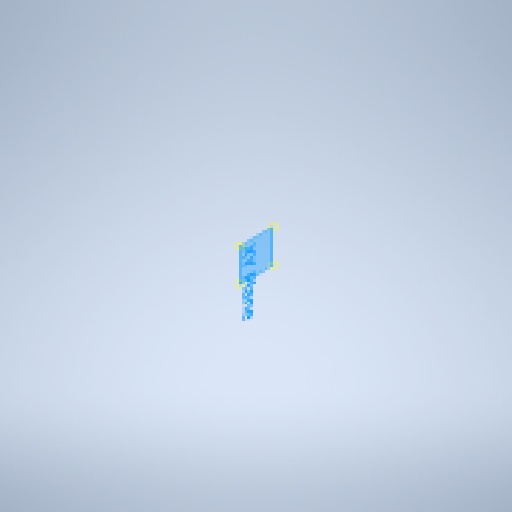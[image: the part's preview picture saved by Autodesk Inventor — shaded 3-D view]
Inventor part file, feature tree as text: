
AUTODESK INVENTOR PART (.ipt)
format: ipt  version: 2023 (Build 270158000, 158)  size: 151,040 bytes
history: native  units: mm
features: other x3, extrude x2, sketch x2, plane x1, chamfer x1, reference x1
ambient origin geometry x8: Origin, YZ Plane, XZ Plane, XY Plane, X Axis, Y Axis, Z Axis, Center Point
bodies: Solid1 (feature_tree)
feature tree (10):
  plane  "Work Plane1"
  extrude  "Extrusion1"  Depth=24.6mm
  extrude  "Extrusion2"  Depth=2.4mm TaperAngle=30.0deg
  chamfer  "Chamfer1"  [1 undecoded]
  sketch  "Sketch1"  dims[d0=24.6mm d1=0.0mm d2=5.9mm]
  reference  "Reference1"
  sketch  "Sketch2"  dims[d3=2.4mm d4=0.0mm d5=2.0mm d6=2.0mm d7=30.0deg]
  parser-record x1  (decoder bookkeeping rows leaked as tree rows — omitted from the tree; the rows remain in map.json)
  other  "Assembly_V6.iam"
  other  "mouldingPlate_V6:1"
note: 1 required parameter value undecoded (feature->parameter linkage not recoverable at this tier; creation-order binding heuristic only, values carry confidence <= 0.55)
note: 1 file-system path scrubbed to <path> (originals preserved in map.json)
